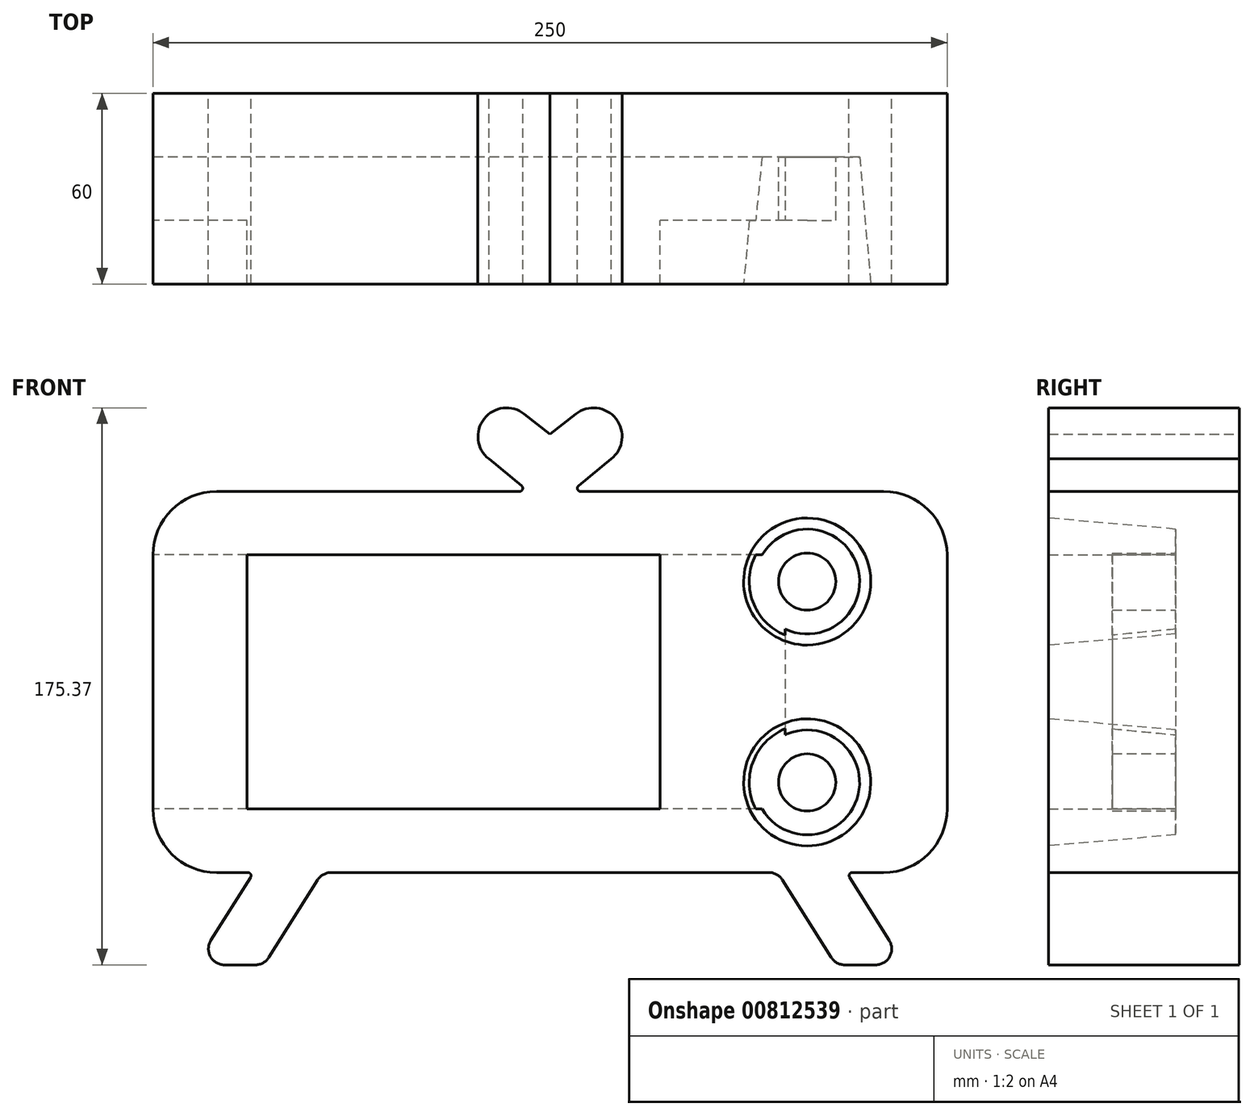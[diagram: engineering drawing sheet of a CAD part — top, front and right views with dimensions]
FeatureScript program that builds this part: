
annotation { "Feature Type Name" : "Feature", "Feature Type Description" : "" }
export const myFeature = defineFeature(function(context is Context, id is Id, definition is map)
    precondition{}
    {
        {
            var Q0;
            Q0=qCreatedBy(makeId("Front.planeOp"),FACE);
            var sketch = newSketch(context, id + "F0", { "sketchPlane" : qUnion([Q0])});
            skLineSegment(sketch, "E0.bottom", {"start": v(65, 40) * mm, "end": v(-65, 40) * mm});
            skLineSegment(sketch, "E0.top", {"start": v(65, -40) * mm, "end": v(-65, -40) * mm});
            skLineSegment(sketch, "E0.left", {"start": v(65, 40) * mm, "end": v(65, -40) * mm});
            skLineSegment(sketch, "E0.right", {"start": v(-65, 40) * mm, "end": v(-65, -40) * mm});
            skPoint(sketch, "E0.middle", {"position": v(0, 0) * mm});
            skSolve(sketch);
        }
        {
            var Q0;
            Q0=makeQuery(id+"F0.imprint","IMPRINT",FACE,{"disambiguationData":[TD([[makeQuery(id+"F0.imprint","IMPRINT",EDGE,{"derivedFrom":sQuery(id+"F0.wireOp",EDGE,"E0.bottom")}),1.0]])]});
            var sketch = newSketch(context, id + "F1", { "sketchPlane" : qUnion([Q0])});
            skLineSegment(sketch, "E1", {"start": v(30.36, 118.63) * mm, "end": v(30.36, -117.83) * mm, "construction": true});
            skLineSegment(sketch, "E2", {"start": v(0, 0) * mm, "end": v(207.4, 0) * mm, "construction": true});
            skSolve(sketch);
        }
        {
            var Q0;
            Q0=qCreatedBy(makeId("Front.planeOp"),FACE);
            var sketch = newSketch(context, id + "F2", { "sketchPlane" : qUnion([Q0])});
            skLineSegment(sketch, "E3.bottom", {"start": v(-74.64, -60) * mm, "end": v(-64.77, -60) * mm});
            skLineSegment(sketch, "E3.top", {"start": v(-74.64, 60) * mm, "end": v(20.76, 60) * mm});
            skLineSegment(sketch, "E3.left", {"start": v(-94.64, -40) * mm, "end": v(-94.64, 40) * mm});
            skLineSegment(sketch, "E3.right", {"start": v(155.36, -40) * mm, "end": v(155.36, 40) * mm});
            skPoint(sketch, "E4.visualSharp", {"position": v(-94.64, 60) * mm});
            skArc(sketch, "E4.filletArc", {"start": v(-74.64, 60) * mm, "mid": v(-88.78, 54.14) * mm, "end": v(-94.64, 40) * mm});
            skPoint(sketch, "E5.visualSharp", {"position": v(-94.64, -60) * mm});
            skArc(sketch, "E5.filletArc", {"start": v(-94.64, -40) * mm, "mid": v(-88.78, -54.14) * mm, "end": v(-74.64, -60) * mm});
            skPoint(sketch, "E6.visualSharp", {"position": v(155.36, 60) * mm});
            skArc(sketch, "E6.filletArc", {"start": v(155.36, 40) * mm, "mid": v(149.5, 54.14) * mm, "end": v(135.36, 60) * mm});
            skPoint(sketch, "E7.visualSharp", {"position": v(155.36, -60) * mm});
            skArc(sketch, "E7.filletArc", {"start": v(135.36, -60) * mm, "mid": v(149.5, -54.14) * mm, "end": v(155.36, -40) * mm});
            skLineSegment(sketch, "E8", {"start": v(30.36, 77.98) * mm, "end": v(22.25, 84.37) * mm});
            skPoint(sketch, "E8.startSnap0", {"position": v(30.36, 60) * mm});
            skLineSegment(sketch, "E9", {"start": v(21.4, 61.77) * mm, "end": v(11.1, 70.22) * mm});
            skArc(sketch, "E10", {"start": v(22.25, 84.37) * mm, "mid": v(9.6, 82.87) * mm, "end": v(11.1, 70.22) * mm});
            skLineSegment(sketch, "E11.MirrorCS", {"start": v(30.36, 77.98) * mm, "end": v(38.47, 84.37) * mm});
            skArc(sketch, "E12.MirrorCS", {"start": v(38.47, 84.37) * mm, "mid": v(51.13, 82.87) * mm, "end": v(49.63, 70.22) * mm});
            skLineSegment(sketch, "E13.MirrorCS", {"start": v(39.32, 61.77) * mm, "end": v(49.63, 70.22) * mm});
            skLineSegment(sketch, "E14.trimOffspring", {"start": v(39.96, 60) * mm, "end": v(135.36, 60) * mm});
            skLineSegment(sketch, "E15", {"start": v(-63.93, -61.53) * mm, "end": v(-76.42, -81.4) * mm});
            skLineSegment(sketch, "E16", {"start": v(-72.19, -89.06) * mm, "end": v(-62.38, -89.06) * mm});
            skLineSegment(sketch, "E17", {"start": v(-58.15, -86.72) * mm, "end": v(-42.82, -62.34) * mm});
            skLineSegment(sketch, "E18.MirrorCS", {"start": v(118.87, -86.72) * mm, "end": v(103.54, -62.34) * mm});
            skLineSegment(sketch, "E19.MirrorCS", {"start": v(124.65, -61.53) * mm, "end": v(137.14, -81.4) * mm});
            skLineSegment(sketch, "E20.MirrorCS", {"start": v(132.9, -89.06) * mm, "end": v(123.1, -89.06) * mm});
            skLineSegment(sketch, "E21.trimOffspring", {"start": v(-38.58, -60) * mm, "end": v(99.3, -60) * mm});
            skLineSegment(sketch, "E22.trimOffspring", {"start": v(125.5, -60) * mm, "end": v(135.36, -60) * mm});
            skPoint(sketch, "E23.visualSharp", {"position": v(-59.62, -89.06) * mm});
            skArc(sketch, "E23.filletArc", {"start": v(-62.38, -89.06) * mm, "mid": v(-59.97, -88.44) * mm, "end": v(-58.15, -86.72) * mm});
            skPoint(sketch, "E24.visualSharp", {"position": v(-81.24, -89.06) * mm});
            skArc(sketch, "E24.filletArc", {"start": v(-76.42, -81.4) * mm, "mid": v(-76.56, -86.48) * mm, "end": v(-72.19, -89.06) * mm});
            skPoint(sketch, "E25.visualSharp", {"position": v(141.96, -89.06) * mm});
            skArc(sketch, "E25.filletArc", {"start": v(132.9, -89.06) * mm, "mid": v(137.29, -86.48) * mm, "end": v(137.14, -81.4) * mm});
            skPoint(sketch, "E26.visualSharp", {"position": v(120.34, -89.06) * mm});
            skArc(sketch, "E26.filletArc", {"start": v(118.87, -86.72) * mm, "mid": v(120.69, -88.44) * mm, "end": v(123.1, -89.06) * mm});
            skPoint(sketch, "E27.visualSharp", {"position": v(102.07, -60) * mm});
            skArc(sketch, "E27.filletArc", {"start": v(103.54, -62.34) * mm, "mid": v(101.72, -60.62) * mm, "end": v(99.3, -60) * mm});
            skPoint(sketch, "E28.visualSharp", {"position": v(-41.35, -60) * mm});
            skArc(sketch, "E28.filletArc", {"start": v(-38.58, -60) * mm, "mid": v(-41, -60.62) * mm, "end": v(-42.82, -62.34) * mm});
            skPoint(sketch, "E29.visualSharp", {"position": v(123.68, -60) * mm});
            skArc(sketch, "E29.filletArc", {"start": v(125.5, -60) * mm, "mid": v(124.62, -60.52) * mm, "end": v(124.65, -61.53) * mm});
            skPoint(sketch, "E30.visualSharp", {"position": v(-62.96, -60) * mm});
            skArc(sketch, "E30.filletArc", {"start": v(-63.93, -61.53) * mm, "mid": v(-63.9, -60.52) * mm, "end": v(-64.77, -60) * mm});
            skPoint(sketch, "E31.visualSharp", {"position": v(37.16, 60) * mm});
            skArc(sketch, "E31.filletArc", {"start": v(39.32, 61.77) * mm, "mid": v(39.02, 60.66) * mm, "end": v(39.96, 60) * mm});
            skPoint(sketch, "E32.visualSharp", {"position": v(23.56, 60) * mm});
            skArc(sketch, "E32.filletArc", {"start": v(20.76, 60) * mm, "mid": v(21.7, 60.66) * mm, "end": v(21.4, 61.77) * mm});
            skSolve(sketch);
        }
        {
            var Q0;
            Q0=makeQuery(id+"F2.imprint","IMPRINT",FACE,{"disambiguationData":[TD([[makeQuery(id+"F2.imprint","IMPRINT",EDGE,{"derivedFrom":sQuery(id+"F2.wireOp",EDGE,"E3.bottom")}),1.0]])]});
            extrude(context, id + "F3", {"entities" : qUnion([Q0]), "endBound" : BoundingType.SYMMETRIC, "depth" : 60 * mm, "offsetDistance" : 25 * mm});
        }
        {
            var Q0;
            Q0=makeQuery(id+"F3.opExtrude","SWEPT_FACE",FACE,{"disambiguationData":[OSD([sQuery(id+"F2.wireOp",EDGE,"E3.left")])]});
            var sketch = newSketch(context, id + "F4", { "sketchPlane" : qUnion([Q0])});
            skLineSegment(sketch, "E33.bottom", {"start": v(10, 40) * mm, "end": v(-10, 40) * mm});
            skLineSegment(sketch, "E33.top", {"start": v(10, -40) * mm, "end": v(-10, -40) * mm});
            skLineSegment(sketch, "E33.left", {"start": v(10, 40) * mm, "end": v(10, -40) * mm});
            skLineSegment(sketch, "E33.right", {"start": v(-10, 40) * mm, "end": v(-10, -40) * mm});
            skPoint(sketch, "E33.middle", {"position": v(0, 0) * mm});
            skSolve(sketch);
        }
        {
            var Q0;
            Q0=makeQuery(id+"F4.imprint","IMPRINT",FACE,{"disambiguationData":[TD([[makeQuery(id+"F4.imprint","IMPRINT",EDGE,{"derivedFrom":sQuery(id+"F4.wireOp",EDGE,"E33.bottom")}),1.0]])]});
            extrude(context, id + "F5", {"entities" : qUnion([Q0]), "operationType" : NewBodyOperationType.REMOVE, "oppositeDirection" : true, "depth" : 199 * mm, "offsetDistance" : 25 * mm});
        }
        {
            var Q0;
            Q0=makeQuery(id+"F3.opExtrude","CAP_FACE",FACE,{"disambiguationData":[OSD([sQuery(id+"F2.wireOp",EDGE,"E3.bottom"),sQuery(id+"F2.wireOp",EDGE,"E3.top"),sQuery(id+"F2.wireOp",EDGE,"E3.left"),sQuery(id+"F2.wireOp",EDGE,"E3.right"),sQuery(id+"F2.wireOp",EDGE,"E4.filletArc"),sQuery(id+"F2.wireOp",EDGE,"E5.filletArc"),sQuery(id+"F2.wireOp",EDGE,"E6.filletArc"),sQuery(id+"F2.wireOp",EDGE,"E7.filletArc"),sQuery(id+"F2.wireOp",EDGE,"E8"),sQuery(id+"F2.wireOp",EDGE,"E9"),sQuery(id+"F2.wireOp",EDGE,"E10"),sQuery(id+"F2.wireOp",EDGE,"E11.MirrorCS"),sQuery(id+"F2.wireOp",EDGE,"E12.MirrorCS"),sQuery(id+"F2.wireOp",EDGE,"E13.MirrorCS"),sQuery(id+"F2.wireOp",EDGE,"E14.trimOffspring"),sQuery(id+"F2.wireOp",EDGE,"E15"),sQuery(id+"F2.wireOp",EDGE,"E16"),sQuery(id+"F2.wireOp",EDGE,"E17"),sQuery(id+"F2.wireOp",EDGE,"E18.MirrorCS"),sQuery(id+"F2.wireOp",EDGE,"E19.MirrorCS"),sQuery(id+"F2.wireOp",EDGE,"E20.MirrorCS"),sQuery(id+"F2.wireOp",EDGE,"E21.trimOffspring"),sQuery(id+"F2.wireOp",EDGE,"E22.trimOffspring"),sQuery(id+"F2.wireOp",EDGE,"E23.filletArc"),sQuery(id+"F2.wireOp",EDGE,"E24.filletArc"),sQuery(id+"F2.wireOp",EDGE,"E25.filletArc"),sQuery(id+"F2.wireOp",EDGE,"E26.filletArc"),sQuery(id+"F2.wireOp",EDGE,"E27.filletArc"),sQuery(id+"F2.wireOp",EDGE,"E28.filletArc"),sQuery(id+"F2.wireOp",EDGE,"E29.filletArc"),sQuery(id+"F2.wireOp",EDGE,"E30.filletArc"),sQuery(id+"F2.wireOp",EDGE,"E31.filletArc"),sQuery(id+"F2.wireOp",EDGE,"E32.filletArc")])],"isStart":false});
            var sketch = newSketch(context, id + "F6", { "sketchPlane" : qUnion([Q0])});
            skCircle(sketch, "E34", {"center": v(111.31, 31.61) * mm, "radius": 20 * mm});
            skCircle(sketch, "E35.MirrorC", {"center": v(111.31, -31.61) * mm, "radius": 20 * mm});
            skSolve(sketch);
        }
        {
            var Q0;
            Q0 = qSketchRegion(id + "F6", true);
            extrude(context, id + "F7", {"entities" : qUnion([Q0]), "operationType" : NewBodyOperationType.REMOVE, "oppositeDirection" : true, "depth" : 40 * mm, "offsetDistance" : 25 * mm, "hasDraft" : true, "draftAngle" : 5 * degree, "draftPullDirection" : true});
        }
        {
            var Q0;
            Q0 = qSketchRegion(id + "F0", true);
            extrude(context, id + "F8", {"entities" : qUnion([Q0]), "operationType" : NewBodyOperationType.REMOVE, "depth" : 43 * mm, "offsetDistance" : 25 * mm});
        }
        {
            var Q0;
            Q0=makeQuery(id+"F7.boolean.opBoolean","MERGE",FACE,{"derivedFrom":[makeQuery(id+"F5.boolean.opBoolean","COPY",FACE,{"derivedFrom":makeQuery(id+"F5.opExtrude","SWEPT_FACE",FACE,{"disambiguationData":[OSD([sQuery(id+"F4.wireOp",EDGE,"E33.right")])]})}),makeQuery(id+"F7.opExtrude","CAP_FACE",FACE,{"disambiguationData":[OSD([sQuery(id+"F6.wireOp",EDGE,"E34")])],"isStart":false}),makeQuery(id+"F7.opExtrude","CAP_FACE",FACE,{"disambiguationData":[OSD([sQuery(id+"F6.wireOp",EDGE,"E35.MirrorC")])],"isStart":false})]});
            var sketch = newSketch(context, id + "F9", { "sketchPlane" : qUnion([Q0])});
            skCircle(sketch, "E36", {"center": v(111.31, 31.61) * mm, "radius": 9 * mm});
            skCircle(sketch, "E37.MirrorC", {"center": v(111.31, -31.61) * mm, "radius": 9 * mm});
            skSolve(sketch);
        }
        {
            var Q0;
            Q0 = qSketchRegion(id + "F9", true);
            extrude(context, id + "F10", {"entities" : qUnion([Q0]), "operationType" : NewBodyOperationType.ADD, "depth" : 20 * mm, "offsetDistance" : 25 * mm});
        }
    });
